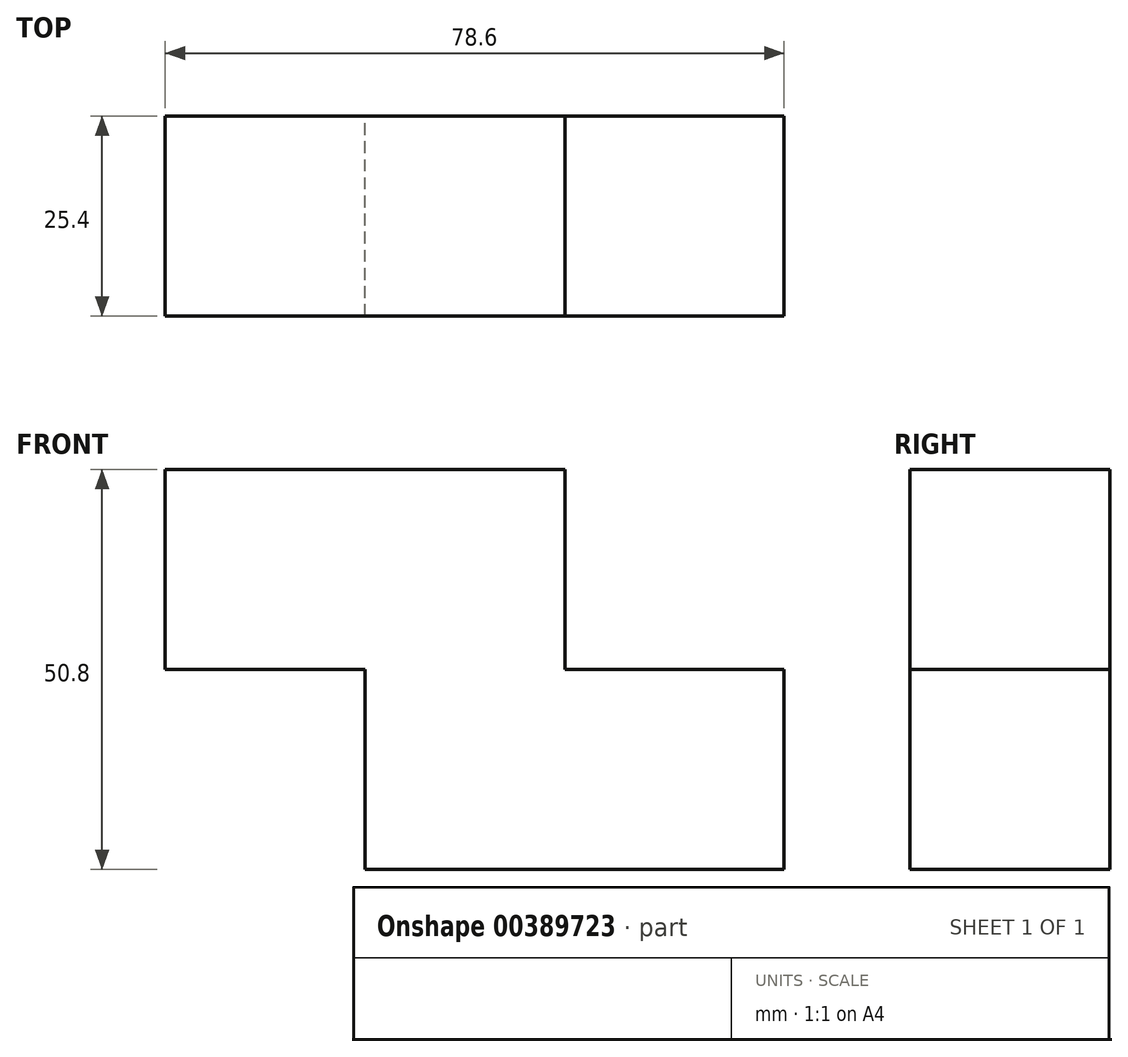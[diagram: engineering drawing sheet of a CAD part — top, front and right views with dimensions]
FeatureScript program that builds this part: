
annotation { "Feature Type Name" : "Feature", "Feature Type Description" : "" }
export const myFeature = defineFeature(function(context is Context, id is Id, definition is map)
    precondition{}
    {
        {
            var Q0;
            Q0=qCreatedBy(makeId("Front.planeOp"),FACE);
            var sketch = newSketch(context, id + "F0", { "sketchPlane" : qUnion([Q0])});
            skLineSegment(sketch, "E0.bottom", {"start": v(0, 0) * mm, "end": v(-25.4, 0) * mm});
            skLineSegment(sketch, "E0.top", {"start": v(0, 25.4) * mm, "end": v(-25.4, 25.4) * mm});
            skLineSegment(sketch, "E0.left", {"start": v(0, 0) * mm, "end": v(0, 25.4) * mm});
            skLineSegment(sketch, "E0.right", {"start": v(-25.4, 0) * mm, "end": v(-25.4, 25.4) * mm});
            skLineSegment(sketch, "E1.bottom", {"start": v(0, 0) * mm, "end": v(25.4, 0) * mm});
            skLineSegment(sketch, "E1.top", {"start": v(0, 25.4) * mm, "end": v(25.4, 25.4) * mm});
            skLineSegment(sketch, "E1.right", {"start": v(25.4, 0) * mm, "end": v(25.4, 25.4) * mm});
            skLineSegment(sketch, "E2.bottom", {"start": v(-25.4, 0) * mm, "end": v(0, 0) * mm});
            skLineSegment(sketch, "E2.top", {"start": v(-25.4, -25.4) * mm, "end": v(0, -25.4) * mm});
            skLineSegment(sketch, "E2.left", {"start": v(-25.4, 0) * mm, "end": v(-25.4, -25.4) * mm});
            skLineSegment(sketch, "E2.right", {"start": v(0, 0) * mm, "end": v(0, -25.4) * mm});
            skLineSegment(sketch, "E3.bottom", {"start": v(0, 0) * mm, "end": v(25.45, 0) * mm});
            skLineSegment(sketch, "E3.top", {"start": v(0, -25.4) * mm, "end": v(25.45, -25.4) * mm});
            skLineSegment(sketch, "E3.right", {"start": v(25.45, 0) * mm, "end": v(25.45, -25.4) * mm});
            skLineSegment(sketch, "E4.bottom", {"start": v(25.45, -25.4) * mm, "end": v(53.2, -25.4) * mm});
            skLineSegment(sketch, "E4.top", {"start": v(25.45, 0) * mm, "end": v(53.2, 0) * mm});
            skLineSegment(sketch, "E4.left", {"start": v(25.45, -25.4) * mm, "end": v(25.45, 0) * mm});
            skLineSegment(sketch, "E4.right", {"start": v(53.2, -25.4) * mm, "end": v(53.2, 0) * mm});
            skSolve(sketch);
        }
        {
            var Q0;
            Q0=makeQuery(id+"F0.imprint","IMPRINT",FACE,{"disambiguationData":[TD([[makeQuery(id+"F0.imprint","IMPRINT",EDGE,{"derivedFrom":sQuery(id+"F0.wireOp",EDGE,"E2.bottom")}),-1.0]])]});
            var Q1;
            Q1=makeQuery(id+"F0.imprint","IMPRINT",FACE,{"disambiguationData":[TD([[makeQuery(id+"F0.imprint","IMPRINT",EDGE,{"derivedFrom":sQuery(id+"F0.wireOp",EDGE,"E3.top")}),1.0]])]});
            extrude(context, id + "F1", {"entities" : qUnion([Q0, Q1]), "depth" : 25.4 * mm});
        }
        {
            var Q0;
            Q0=makeQuery(id+"F0.imprint","IMPRINT",FACE,{"disambiguationData":[TD([[makeQuery(id+"F0.imprint","IMPRINT",EDGE,{"derivedFrom":sQuery(id+"F0.wireOp",EDGE,"E0.top")}),1.0]])]});
            var Q1;
            Q1=makeQuery(id+"F0.imprint","IMPRINT",FACE,{"disambiguationData":[TD([[makeQuery(id+"F0.imprint","IMPRINT",EDGE,{"derivedFrom":sQuery(id+"F0.wireOp",EDGE,"E1.top")}),-1.0]])]});
            var Q2;
            Q2=makeQuery(id+"F0.imprint","IMPRINT",FACE,{"disambiguationData":[TD([[makeQuery(id+"F0.imprint","IMPRINT",EDGE,{"derivedFrom":sQuery(id+"F0.wireOp",EDGE,"E4.bottom")}),1.0]])]});
            extrude(context, id + "F2", {"entities" : qUnion([Q0, Q1, Q2]), "operationType" : NewBodyOperationType.ADD, "depth" : 25.4 * mm});
        }
    });
